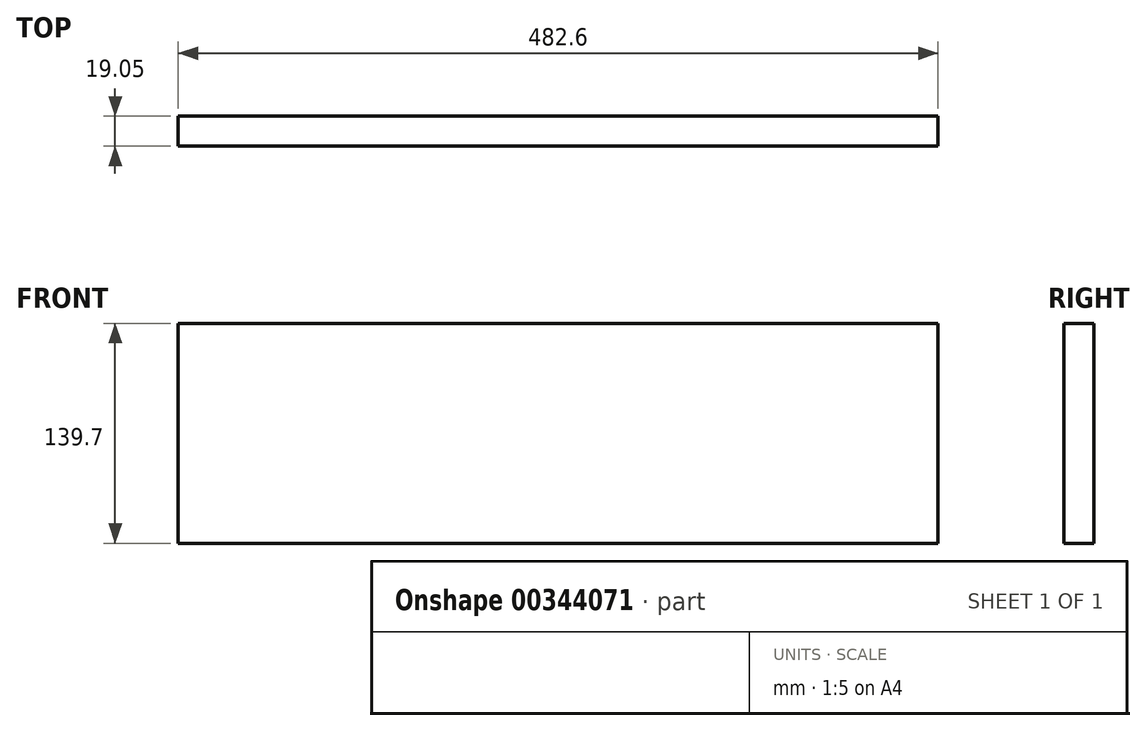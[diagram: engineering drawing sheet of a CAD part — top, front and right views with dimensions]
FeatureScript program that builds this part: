
annotation { "Feature Type Name" : "Feature", "Feature Type Description" : "" }
export const myFeature = defineFeature(function(context is Context, id is Id, definition is map)
    precondition{}
    {
        {
            var Q0;
            Q0=qCreatedBy(makeId("Front.planeOp"),FACE);
            var sketch = newSketch(context, id + "F0", { "sketchPlane" : qUnion([Q0])});
            skLineSegment(sketch, "E0.bottom", {"start": v(0, 0) * mm, "end": v(482.6, 0) * mm});
            skLineSegment(sketch, "E0.top", {"start": v(0, 139.7) * mm, "end": v(482.6, 139.7) * mm});
            skLineSegment(sketch, "E0.left", {"start": v(0, 0) * mm, "end": v(0, 139.7) * mm});
            skLineSegment(sketch, "E0.right", {"start": v(482.6, 0) * mm, "end": v(482.6, 139.7) * mm});
            skSolve(sketch);
        }
        {
            var Q0;
            Q0=qSketchRegion(id+"F0",true);
            extrude(context, id + "F1", {"entities" : qUnion([Q0]), "depth" : 19.05 * mm});
        }
    });
